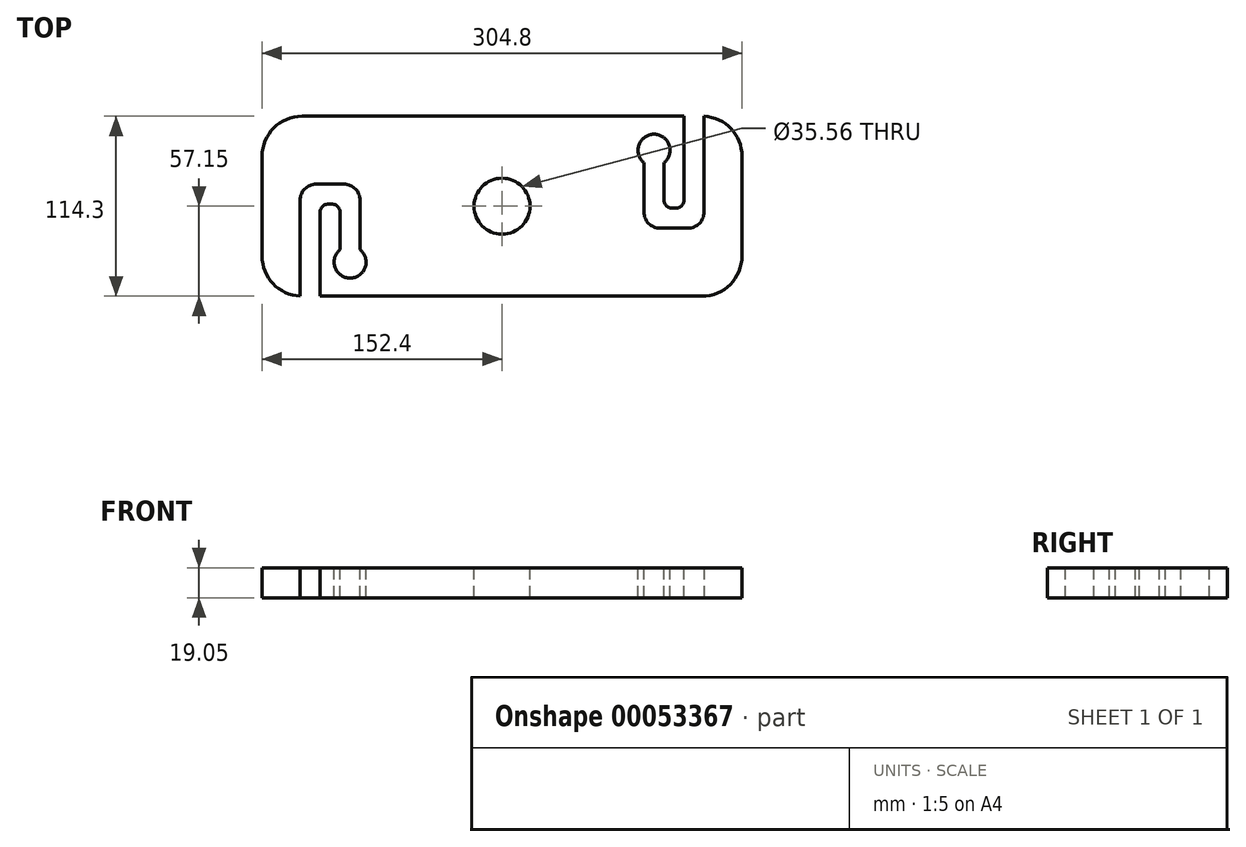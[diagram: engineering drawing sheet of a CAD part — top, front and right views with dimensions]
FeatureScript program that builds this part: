
annotation { "Feature Type Name" : "Feature", "Feature Type Description" : "" }
export const myFeature = defineFeature(function(context is Context, id is Id, definition is map)
    precondition{}
    {
        {
            var Q0;
            Q0=qCreatedBy(makeId("Top.planeOp"),FACE);
            var sketch = newSketch(context, id + "F0", { "sketchPlane" : qUnion([Q0])});
            skLineSegment(sketch, "E0.rect.bottom", {"start": v(127, 57.15) * mm, "end": v(-127, 57.15) * mm});
            skLineSegment(sketch, "E0.rect.top", {"start": v(127, -57.15) * mm, "end": v(-127, -57.15) * mm});
            skLineSegment(sketch, "E0.rect.left", {"start": v(152.4, 31.75) * mm, "end": v(152.4, -31.75) * mm});
            skLineSegment(sketch, "E0.rect.right", {"start": v(-152.4, 31.75) * mm, "end": v(-152.4, -31.75) * mm});
            skPoint(sketch, "E0.rect.middle", {"position": v(0, 0) * mm});
            skPoint(sketch, "E1.visualSharp", {"position": v(-152.4, 57.15) * mm});
            skArc(sketch, "E1.filletArc", {"start": v(-127, 57.15) * mm, "mid": v(-144.96, 49.71) * mm, "end": v(-152.4, 31.75) * mm});
            skPoint(sketch, "E2.visualSharp", {"position": v(152.4, 57.15) * mm});
            skArc(sketch, "E2.filletArc", {"start": v(152.4, 31.75) * mm, "mid": v(144.96, 49.71) * mm, "end": v(127, 57.15) * mm});
            skPoint(sketch, "E3.visualSharp", {"position": v(152.4, -57.15) * mm});
            skArc(sketch, "E3.filletArc", {"start": v(127, -57.15) * mm, "mid": v(144.96, -49.71) * mm, "end": v(152.4, -31.75) * mm});
            skPoint(sketch, "E4.visualSharp", {"position": v(-152.4, -57.15) * mm});
            skArc(sketch, "E4.filletArc", {"start": v(-152.4, -31.75) * mm, "mid": v(-144.96, -49.71) * mm, "end": v(-127, -57.15) * mm});
            skSolve(sketch);
        }
        {
            var Q0;
            Q0=qSketchRegion(id+"F0",true);
            extrude(context, id + "F1", {"entities" : qUnion([Q0]), "depth" : 19.05 * mm});
        }
        {
            var Q0;
            Q0=makeQuery(id+"F1.opExtrude","CAP_FACE",FACE,{"disambiguationData":[OSD([sQuery(id+"F0.wireOp",EDGE,"E0.rect.bottom"),sQuery(id+"F0.wireOp",EDGE,"E0.rect.top"),sQuery(id+"F0.wireOp",EDGE,"E0.rect.left"),sQuery(id+"F0.wireOp",EDGE,"E0.rect.right"),sQuery(id+"F0.wireOp",EDGE,"E1.filletArc"),sQuery(id+"F0.wireOp",EDGE,"E2.filletArc"),sQuery(id+"F0.wireOp",EDGE,"E3.filletArc"),sQuery(id+"F0.wireOp",EDGE,"E4.filletArc")])],"isStart":false});
            var sketch = newSketch(context, id + "F2", { "sketchPlane" : qUnion([Q0])});
            skCircle(sketch, "E5", {"center": v(0, 0) * mm, "radius": 17.78 * mm});
            skSolve(sketch);
        }
        {
            var Q0;
            Q0=qSketchRegion(id+"F2",true);
            extrude(context, id + "F3", {"entities" : qUnion([Q0]), "operationType" : NewBodyOperationType.REMOVE, "endBound" : BoundingType.THROUGH_ALL, "oppositeDirection" : true, "depth" : 25.4 * mm});
        }
        {
            var Q0;
            Q0=makeQuery(id+"F1.opExtrude","CAP_FACE",FACE,{"disambiguationData":[OSD([sQuery(id+"F0.wireOp",EDGE,"E0.rect.bottom"),sQuery(id+"F0.wireOp",EDGE,"E0.rect.top"),sQuery(id+"F0.wireOp",EDGE,"E0.rect.left"),sQuery(id+"F0.wireOp",EDGE,"E0.rect.right"),sQuery(id+"F0.wireOp",EDGE,"E1.filletArc"),sQuery(id+"F0.wireOp",EDGE,"E2.filletArc"),sQuery(id+"F0.wireOp",EDGE,"E3.filletArc"),sQuery(id+"F0.wireOp",EDGE,"E4.filletArc")])],"isStart":false});
            var sketch = newSketch(context, id + "F4", { "sketchPlane" : qUnion([Q0])});
            skLineSegment(sketch, "E6", {"start": v(-128.27, -57.15) * mm, "end": v(-128.27, 3.8) * mm});
            skLineSegment(sketch, "E7", {"start": v(-115.57, -57.15) * mm, "end": v(-115.57, -3.81) * mm});
            skLineSegment(sketch, "E8", {"start": v(128.27, 57.15) * mm, "end": v(128.27, -3.81) * mm});
            skLineSegment(sketch, "E9", {"start": v(115.57, 57.15) * mm, "end": v(115.57, 3.81) * mm});
            skLineSegment(sketch, "E10", {"start": v(-127, -57.15) * mm, "end": v(-115.57, -57.15) * mm});
            skLineSegment(sketch, "E11", {"start": v(128.27, 57.15) * mm, "end": v(115.57, 57.15) * mm});
            skLineSegment(sketch, "E12", {"start": v(118.11, -13.97) * mm, "end": v(100.33, -13.97) * mm});
            skLineSegment(sketch, "E13", {"start": v(90.17, -3.81) * mm, "end": v(90.17, 27.63) * mm});
            skLineSegment(sketch, "E14", {"start": v(110.49, -1.27) * mm, "end": v(107.95, -1.27) * mm});
            skLineSegment(sketch, "E15", {"start": v(102.87, 3.81) * mm, "end": v(102.87, 27.63) * mm});
            skLineSegment(sketch, "E16", {"start": v(-118.11, 13.97) * mm, "end": v(-100.33, 13.97) * mm});
            skLineSegment(sketch, "E17", {"start": v(-90.17, 3.81) * mm, "end": v(-90.17, -27.63) * mm});
            skLineSegment(sketch, "E18", {"start": v(-110.5, 1.27) * mm, "end": v(-107.95, 1.27) * mm});
            skLineSegment(sketch, "E19", {"start": v(-102.87, -3.81) * mm, "end": v(-102.87, -27.63) * mm});
            skPoint(sketch, "E20.visualSharp", {"position": v(-128.27, 13.97) * mm});
            skArc(sketch, "E20.filletArc", {"start": v(-118.11, 13.97) * mm, "mid": v(-125.3, 11) * mm, "end": v(-128.27, 3.8) * mm});
            skPoint(sketch, "E21.visualSharp", {"position": v(-90.17, 13.97) * mm});
            skArc(sketch, "E21.filletArc", {"start": v(-90.17, 3.81) * mm, "mid": v(-93.15, 11) * mm, "end": v(-100.33, 13.97) * mm});
            skPoint(sketch, "E22.visualSharp", {"position": v(128.27, -13.97) * mm});
            skArc(sketch, "E22.filletArc", {"start": v(118.11, -13.97) * mm, "mid": v(125.3, -11) * mm, "end": v(128.27, -3.81) * mm});
            skPoint(sketch, "E23.visualSharp", {"position": v(90.17, -13.97) * mm});
            skArc(sketch, "E23.filletArc", {"start": v(90.17, -3.81) * mm, "mid": v(93.15, -11) * mm, "end": v(100.33, -13.97) * mm});
            skPoint(sketch, "E24.visualSharp", {"position": v(-115.57, 1.27) * mm});
            skArc(sketch, "E24.filletArc", {"start": v(-110.5, 1.27) * mm, "mid": v(-114.08, -0.22) * mm, "end": v(-115.57, -3.81) * mm});
            skPoint(sketch, "E25.visualSharp", {"position": v(-102.87, 1.27) * mm});
            skArc(sketch, "E25.filletArc", {"start": v(-102.87, -3.81) * mm, "mid": v(-104.36, -0.22) * mm, "end": v(-107.95, 1.27) * mm});
            skPoint(sketch, "E26.visualSharp", {"position": v(102.87, -1.27) * mm});
            skArc(sketch, "E26.filletArc", {"start": v(102.87, 3.81) * mm, "mid": v(104.36, 0.22) * mm, "end": v(107.95, -1.27) * mm});
            skPoint(sketch, "E27.visualSharp", {"position": v(115.57, -1.27) * mm});
            skArc(sketch, "E27.filletArc", {"start": v(110.49, -1.27) * mm, "mid": v(114.08, 0.22) * mm, "end": v(115.57, 3.81) * mm});
            skPoint(sketch, "E28.visualSharp", {"position": v(-90.17, -36.83) * mm});
            skPoint(sketch, "E29.visualSharp", {"position": v(-102.87, -36.83) * mm});
            skPoint(sketch, "E30.visualSharp", {"position": v(90.17, 36.83) * mm});
            skPoint(sketch, "E31.visualSharp", {"position": v(102.87, 36.83) * mm});
            skArc(sketch, "E32", {"start": v(-102.87, -27.63) * mm, "mid": v(-96.52, -45.72) * mm, "end": v(-90.17, -27.63) * mm});
            skArc(sketch, "E33", {"start": v(102.87, 27.63) * mm, "mid": v(96.52, 45.72) * mm, "end": v(90.17, 27.63) * mm});
            skSolve(sketch);
        }
        {
            var Q0;
            Q0=qSketchRegion(id+"F4",true);
            var Q1;
            Q1=makeQuery(id+"F4.imprint","IMPRINT",FACE,{"disambiguationData":[TD([[makeQuery(id+"F4.imprint","IMPRINT",EDGE,{"derivedFrom":sQuery(id+"F4.wireOp",EDGE,"E7")}),1.0]])]});
            extrude(context, id + "F5", {"entities" : qUnion([Q0, Q1]), "operationType" : NewBodyOperationType.REMOVE, "endBound" : BoundingType.THROUGH_ALL, "oppositeDirection" : true, "depth" : 25.4 * mm});
        }
    });
